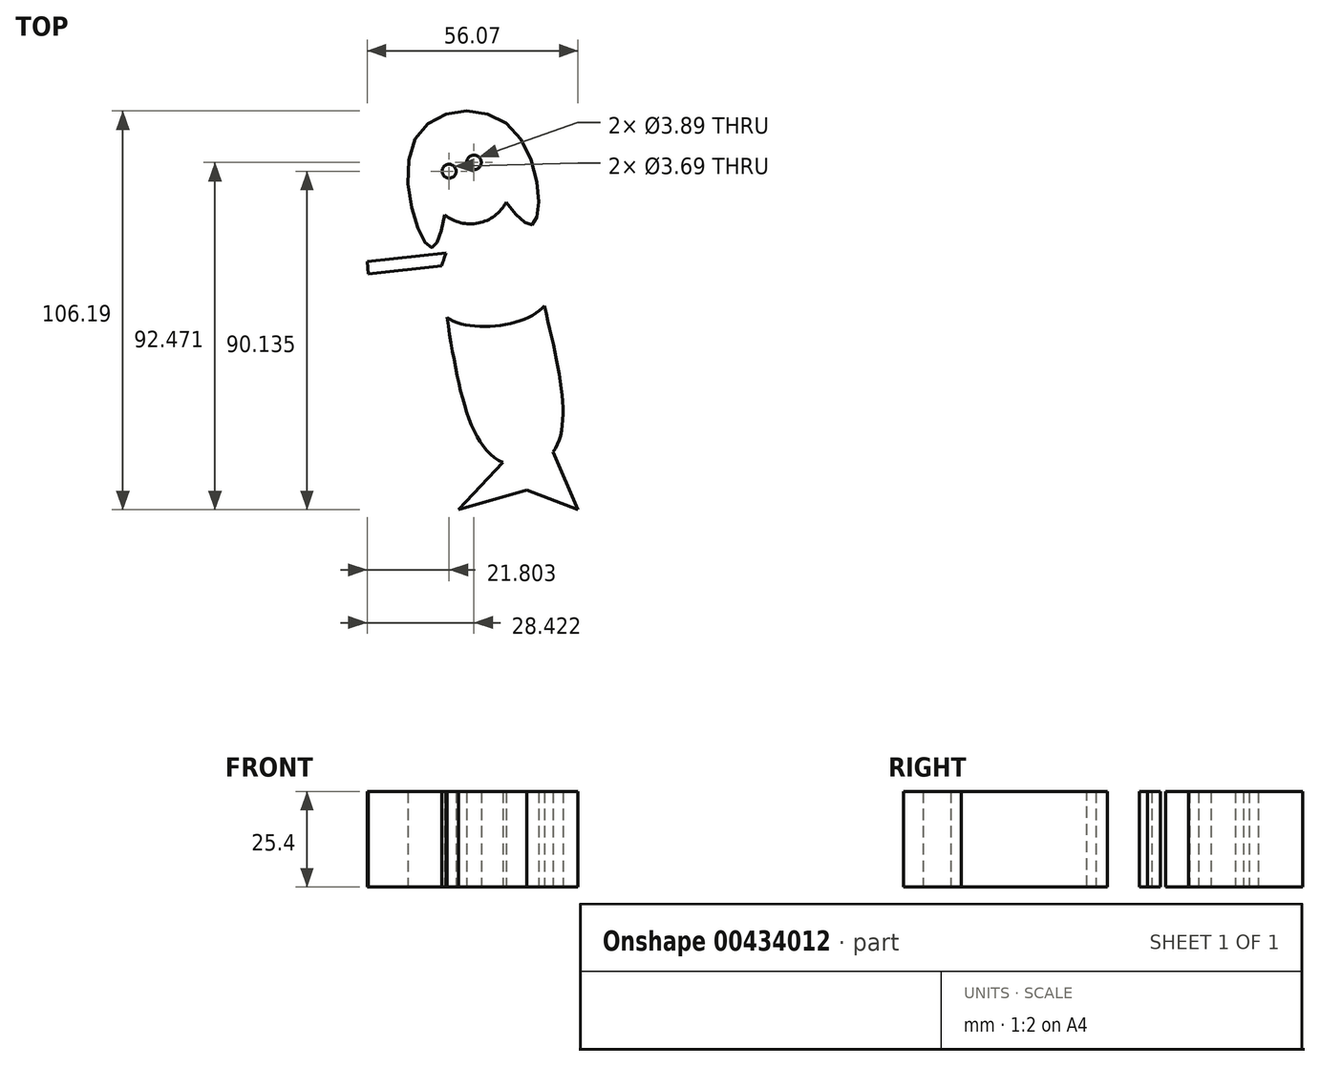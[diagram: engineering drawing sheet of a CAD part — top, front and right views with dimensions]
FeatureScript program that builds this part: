
annotation { "Feature Type Name" : "Feature", "Feature Type Description" : "" }
export const myFeature = defineFeature(function(context is Context, id is Id, definition is map)
    precondition{}
    {
        {
            var Q0;
            Q0=qCreatedBy(makeId("Top.planeOp"),FACE);
            var sketch = newSketch(context, id + "F0", { "sketchPlane" : qUnion([Q0])});
            skCircle(sketch, "E0", {"center": v(27.45, 41.08) * mm, "radius": 10.72 * mm});
            skFitSpline(sketch, "E1", {"points": [v(36.94, 36.1) * mm, v(44.2, 30.37) * mm, v(38.74, 55.68) * mm, v(12.65, 52.76) * mm, v(16.74, 24.14) * mm, v(20.68, 32.76) * mm], "startDerivative": vector(60.4, -75.42) * mm, "endDerivative": vector(22.12, 99.11) * mm});
            skCircle(sketch, "E2", {"center": v(21.8, 44.39) * mm, "radius": 1.85 * mm});
            skCircle(sketch, "E3", {"center": v(28.42, 46.72) * mm, "radius": 1.95 * mm});
            skFitSpline(sketch, "E4", {"points": [v(24.24, 30.84) * mm, v(21.22, 5.45) * mm, v(47.11, 8.57) * mm, v(35.04, 33.48) * mm], "startDerivative": vector(-39.82, -96.37) * mm, "endDerivative": vector(-72.05, 84.36) * mm});
            skFitSpline(sketch, "E5", {"points": [v(21.22, 5.45) * mm, v(34.26, -32.12) * mm, v(49.45, -30.37) * mm, v(47.11, 8.57) * mm], "startDerivative": vector(20.14, -125.99) * mm, "endDerivative": vector(-30.36, 126.59) * mm});
            skLineSegment(sketch, "E6", {"start": v(36.17, -33.18) * mm, "end": v(24.33, -45.75) * mm});
            skLineSegment(sketch, "E7", {"start": v(24.33, -45.75) * mm, "end": v(42.44, -40.5) * mm});
            skLineSegment(sketch, "E8", {"start": v(42.44, -40.5) * mm, "end": v(56.07, -45.75) * mm});
            skLineSegment(sketch, "E9", {"start": v(56.07, -45.75) * mm, "end": v(49.45, -30.37) * mm});
            skLineSegment(sketch, "E10", {"start": v(20.97, 22.6) * mm, "end": v(0, 20.31) * mm});
            skLineSegment(sketch, "E11", {"start": v(0, 20.31) * mm, "end": v(0.35, 17.08) * mm});
            skLineSegment(sketch, "E12", {"start": v(0.35, 17.08) * mm, "end": v(19.89, 19.22) * mm});
            skLineSegment(sketch, "E13", {"start": v(41.2, 26.07) * mm, "end": v(59.19, 31.35) * mm});
            skLineSegment(sketch, "E14", {"start": v(59.19, 31.35) * mm, "end": v(60.74, 27.45) * mm});
            skLineSegment(sketch, "E15", {"start": v(60.74, 27.45) * mm, "end": v(43.23, 23.9) * mm});
            skSolve(sketch);
        }
        {
            var Q0;
            Q0 = qSketchRegion(id + "F0", true);
            extrude(context, id + "F1", {"entities" : qUnion([Q0]), "depth" : 25.4 * mm});
        }
        {
            var Q0;
            Q0 = qSketchRegion(id + "F0", true);
            extrude(context, id + "F2", {"entities" : qUnion([Q0]), "depth" : 25.4 * mm});
        }
    });
